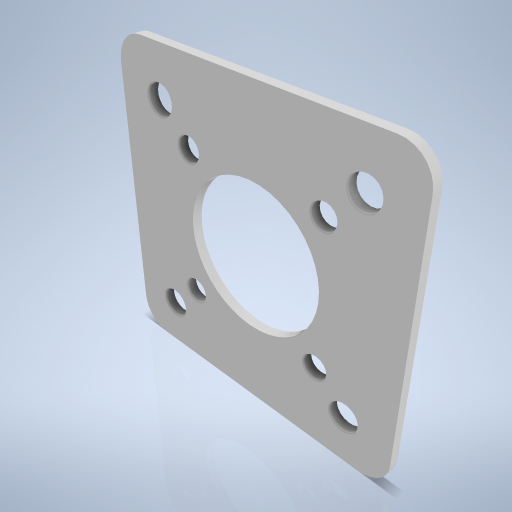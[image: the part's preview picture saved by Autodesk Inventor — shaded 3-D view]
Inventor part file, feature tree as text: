
AUTODESK INVENTOR PART (.ipt)
format: ipt  version: 2024.2 (Build 282272000, 272)  size: 267,776 bytes
history: native  units: mm
features: sketch x3, hole x3, extrude x1, fillet x1
ambient origin geometry x8: Origin, YZ Plane, XZ Plane, XY Plane, X Axis, Y Axis, Z Axis, Center Point
bodies: Volumenkörper1 (feature_tree)
feature tree (8):
  extrude  "Extrusion1"  Depth=62.0mm
  fillet  "Rundung1"  Radius=2.0mm
  sketch  "Skizze2"  dims[d4=6.0mm]
  hole  "Bohrung1"  [1 undecoded]
  hole  "Bohrung2"  [1 undecoded]
  hole  "Bohrung3"  [1 undecoded]
  sketch  "Skizze1"  dims[d0=62.0mm d1=62.0mm d2=2.0mm d3=0.0mm]
  sketch  "Skizze3"  dims[d5=6.0mm d6=6.0mm d7=4.0mm d8=2.0mm d9=90.0deg d10=8.0mm d11=0.0mm d19=29.0mm d20=6.0mm d21=4.0mm d22=2.0mm d23=90.0deg d24=8.0mm d25=0.0mm d26=5.0mm d27=10.0mm d28=4.0mm d29=2.0mm d30=90.0deg d31=14.0mm d32=0.0mm d33=29.0mm d34=14.5mm d35=29.0mm d36=14.5mm d37=42.248mm d38=42.248mm d39=42.248mm]
note: 3 required parameter values undecoded (feature->parameter linkage not recoverable at this tier; creation-order binding heuristic only, values carry confidence <= 0.55)
